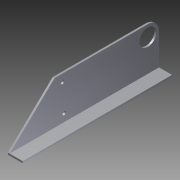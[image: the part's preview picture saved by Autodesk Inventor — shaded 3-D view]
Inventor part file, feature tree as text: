
AUTODESK INVENTOR PART (.ipt)
format: ipt  version: 2012 (Build 160160000, 160)  size: 110,592 bytes
history: native  units: in
note: dims shown in document units (in); Inventor stores cm internally (conversion verified against a paired STEP export)
features: extrude x2, sketch x2
ambient origin geometry x8: Origin, YZ Plane, XZ Plane, XY Plane, X Axis, Y Axis, Z Axis, Center Point
bodies: Solid1 (feature_tree)
feature tree (4):
  extrude  "Extrusion1"  Depth=1.0in
  extrude  "Extrusion2"  Depth=0.125in
  sketch  "Sketch1"  dims[d0=3.0in d1=1.0in]
  sketch  "Sketch2"  dims[d2=0.125in d3=0.125in d4=10.0in d5=0.0in d6=1.0in d7=0.5in d8=3.0in d9=0.5in d10=0.5in d11=0.5in d12=0.5in d13=0.25in d14=0.25in d15=1.0in d16=0.0in d17=0.75in d18=1.125in d19=0.0216in]
